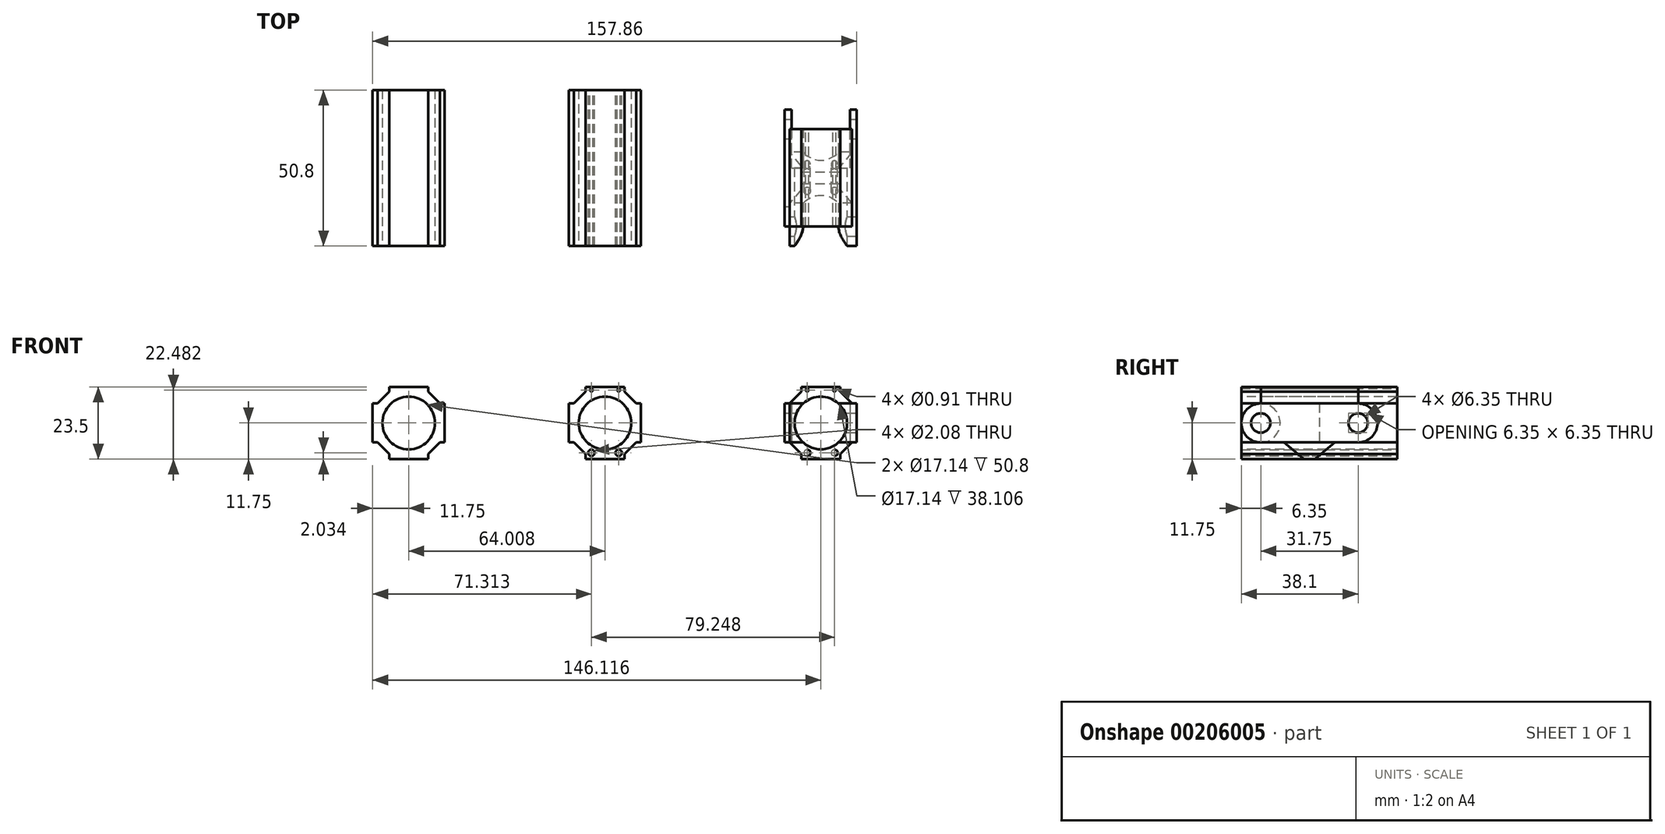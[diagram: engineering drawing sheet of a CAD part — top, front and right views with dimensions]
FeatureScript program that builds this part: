
annotation { "Feature Type Name" : "Feature", "Feature Type Description" : "" }
export const myFeature = defineFeature(function(context is Context, id is Id, definition is map)
    precondition{}
    {
        {
            var Q0;
            Q0=qCreatedBy(makeId("Front.planeOp"),FACE);
            var sketch = newSketch(context, id + "F0", { "sketchPlane" : qUnion([Q0])});
            skCircle(sketch, "E0", {"center": v(0, 0) * mm, "radius": 8.57 * mm});
            skCircle(sketch, "E1", {"center": v(0, 0) * mm, "radius": 11.11 * mm});
            skLineSegment(sketch, "E2", {"start": v(-13.77, 0) * mm, "end": v(14.8, 0) * mm, "construction": true});
            skLineSegment(sketch, "E3", {"start": v(0, 15.5) * mm, "end": v(0, -14.67) * mm, "construction": true});
            skLineSegment(sketch, "E4", {"start": v(-8.57, 0) * mm, "end": v(-8.57, -12.33) * mm, "construction": true});
            skLineSegment(sketch, "E5", {"start": v(8.57, 0) * mm, "end": v(8.57, -11.96) * mm, "construction": true});
            skLineSegment(sketch, "E6.bottom", {"start": v(-8.57, -6.35) * mm, "end": v(-11.75, -6.35) * mm});
            skLineSegment(sketch, "E6.top", {"start": v(-8.57, 6.35) * mm, "end": v(-11.75, 6.35) * mm});
            skLineSegment(sketch, "E6.left", {"start": v(-8.57, -6.35) * mm, "end": v(-8.57, 6.35) * mm});
            skLineSegment(sketch, "E6.right", {"start": v(-11.75, -6.35) * mm, "end": v(-11.75, 6.35) * mm});
            skPoint(sketch, "E7.oppositeSnap0", {"position": v(-10.16, 6.35) * mm});
            skLineSegment(sketch, "E7.bottom", {"start": v(8.57, -6.35) * mm, "end": v(11.75, -6.35) * mm});
            skLineSegment(sketch, "E7.top", {"start": v(8.57, 6.35) * mm, "end": v(11.75, 6.35) * mm});
            skLineSegment(sketch, "E7.left", {"start": v(8.57, -6.35) * mm, "end": v(8.57, 6.35) * mm});
            skLineSegment(sketch, "E7.right", {"start": v(11.75, -6.35) * mm, "end": v(11.75, 6.35) * mm});
            skLineSegment(sketch, "E8", {"start": v(0, 8.57) * mm, "end": v(9.91, 8.57) * mm, "construction": true});
            skLineSegment(sketch, "E9", {"start": v(0, -8.57) * mm, "end": v(9.95, -8.57) * mm, "construction": true});
            skLineSegment(sketch, "E10.bottom", {"start": v(6.35, 8.57) * mm, "end": v(-6.35, 8.57) * mm});
            skLineSegment(sketch, "E10.top", {"start": v(6.35, 11.75) * mm, "end": v(-6.35, 11.75) * mm});
            skLineSegment(sketch, "E10.left", {"start": v(6.35, 8.57) * mm, "end": v(6.35, 11.75) * mm});
            skLineSegment(sketch, "E10.right", {"start": v(-6.35, 8.57) * mm, "end": v(-6.35, 11.75) * mm});
            skPoint(sketch, "E11.oppositeSnap0", {"position": v(-6.35, 10.16) * mm});
            skLineSegment(sketch, "E11.bottom", {"start": v(6.35, -8.57) * mm, "end": v(-6.35, -8.57) * mm});
            skLineSegment(sketch, "E11.top", {"start": v(6.35, -11.75) * mm, "end": v(-6.35, -11.75) * mm});
            skLineSegment(sketch, "E11.left", {"start": v(6.35, -8.57) * mm, "end": v(6.35, -11.75) * mm});
            skLineSegment(sketch, "E11.right", {"start": v(-6.35, -8.57) * mm, "end": v(-6.35, -11.75) * mm});
            skLineSegment(sketch, "E12", {"start": v(-6.35, 10.16) * mm, "end": v(-10.16, 6.35) * mm});
            skLineSegment(sketch, "E13", {"start": v(-10.16, -6.35) * mm, "end": v(-6.35, -10.16) * mm});
            skLineSegment(sketch, "E14", {"start": v(6.35, -10.16) * mm, "end": v(10.16, -6.35) * mm});
            skLineSegment(sketch, "E15", {"start": v(6.35, 10.16) * mm, "end": v(10.16, 6.35) * mm});
            skSolve(sketch);
        }
        {
            var Q0;
            {var subQ4=sQuery(id+"F0.wireOp",EDGE,"E6.right");Q0=makeQuery(id+"F0.imprint","IMPRINT",FACE,{"disambiguationData":[TD([[makeQuery(id+"F0.imprint","IMPRINT",EDGE,{"derivedFrom":subQ4}),-1.0]])]});}
            var Q1;
            {var subQ5=sQuery(id+"F0.wireOp",EDGE,"E15");Q1=makeQuery(id+"F0.imprint","IMPRINT",FACE,{"disambiguationData":[TD([[makeQuery(id+"F0.imprint","IMPRINT",EDGE,{"derivedFrom":subQ5}),-1.0]])]});}
            var Q2;
            {var subQ0=sQuery(id+"F0.wireOp",EDGE,"E7.left");var subQ3=sQuery(id+"F0.wireOp",EDGE,"E0");var subQ4=makeQuery(id+"F0.imprint","INTERSECT",VERTEX,{"derivedFrom":[subQ3,subQ0]});Q2=makeQuery(id+"F0.imprint","IMPRINT",FACE,{"disambiguationData":[TD([[makeQuery(id+"F0.imprint","IMPRINT",EDGE,{"disambiguationData":[TD([[subQ4,1.0]])],"derivedFrom":subQ3}),-1.0]])]});}
            var Q3;
            {var subQ3=sQuery(id+"F0.wireOp",EDGE,"E0");var subQ9=sQuery(id+"F0.wireOp",EDGE,"E10.bottom");var subQ10=makeQuery(id+"F0.imprint","INTERSECT",VERTEX,{"derivedFrom":[subQ3,subQ9]});Q3=makeQuery(id+"F0.imprint","IMPRINT",FACE,{"disambiguationData":[TD([[makeQuery(id+"F0.imprint","IMPRINT",EDGE,{"disambiguationData":[TD([[subQ10,1.0]])],"derivedFrom":subQ3}),-1.0]])]});}
            var Q4;
            {var subQ0=sQuery(id+"F0.wireOp",EDGE,"E10.left");var subQ3=sQuery(id+"F0.wireOp",EDGE,"E1");var subQ4=makeQuery(id+"F0.imprint","INTERSECT",VERTEX,{"derivedFrom":[subQ3,subQ0]});Q4=makeQuery(id+"F0.imprint","IMPRINT",FACE,{"disambiguationData":[TD([[makeQuery(id+"F0.imprint","IMPRINT",EDGE,{"disambiguationData":[TD([[subQ4,-1.0]])],"derivedFrom":subQ3}),1.0]])]});}
            var Q5;
            {var subQ0=sQuery(id+"F0.wireOp",EDGE,"E10.top");Q5=makeQuery(id+"F0.imprint","IMPRINT",FACE,{"disambiguationData":[TD([[makeQuery(id+"F0.imprint","IMPRINT",EDGE,{"derivedFrom":subQ0}),1.0]])]});}
            var Q6;
            {var subQ5=sQuery(id+"F0.wireOp",EDGE,"E12");Q6=makeQuery(id+"F0.imprint","IMPRINT",FACE,{"disambiguationData":[TD([[makeQuery(id+"F0.imprint","IMPRINT",EDGE,{"derivedFrom":subQ5}),1.0]])]});}
            var Q7;
            {var subQ5=sQuery(id+"F0.wireOp",EDGE,"E0");var subQ9=sQuery(id+"F0.wireOp",EDGE,"E10.bottom");var subQ11=makeQuery(id+"F0.imprint","INTERSECT",VERTEX,{"derivedFrom":[subQ5,subQ9]});Q7=makeQuery(id+"F0.imprint","IMPRINT",FACE,{"disambiguationData":[TD([[makeQuery(id+"F0.imprint","IMPRINT",EDGE,{"disambiguationData":[TD([[subQ11,-1.0]])],"derivedFrom":subQ5}),-1.0]])]});}
            var Q8;
            {var subQ0=sQuery(id+"F0.wireOp",EDGE,"E6.left");var subQ7=sQuery(id+"F0.wireOp",EDGE,"E0");var subQ8=makeQuery(id+"F0.imprint","INTERSECT",VERTEX,{"derivedFrom":[subQ7,subQ0]});Q8=makeQuery(id+"F0.imprint","IMPRINT",FACE,{"disambiguationData":[TD([[makeQuery(id+"F0.imprint","IMPRINT",EDGE,{"disambiguationData":[TD([[subQ8,-1.0]])],"derivedFrom":subQ7}),-1.0]])]});}
            var Q9;
            {var subQ5=sQuery(id+"F0.wireOp",EDGE,"E13");Q9=makeQuery(id+"F0.imprint","IMPRINT",FACE,{"disambiguationData":[TD([[makeQuery(id+"F0.imprint","IMPRINT",EDGE,{"derivedFrom":subQ5}),1.0]])]});}
            var Q10;
            {var subQ4=sQuery(id+"F0.wireOp",EDGE,"E6.top");var subQ5=sQuery(id+"F0.wireOp",EDGE,"E1");var subQ6=makeQuery(id+"F0.imprint","INTERSECT",VERTEX,{"derivedFrom":[subQ5,subQ4]});Q10=makeQuery(id+"F0.imprint","IMPRINT",FACE,{"disambiguationData":[TD([[makeQuery(id+"F0.imprint","IMPRINT",EDGE,{"disambiguationData":[TD([[subQ6,-1.0]])],"derivedFrom":subQ5}),1.0]])]});}
            var Q11;
            {var subQ3=sQuery(id+"F0.wireOp",EDGE,"E1");var subQ6=sQuery(id+"F0.wireOp",EDGE,"E11.right");var subQ8=makeQuery(id+"F0.imprint","INTERSECT",VERTEX,{"derivedFrom":[subQ3,subQ6]});Q11=makeQuery(id+"F0.imprint","IMPRINT",FACE,{"disambiguationData":[TD([[makeQuery(id+"F0.imprint","IMPRINT",EDGE,{"disambiguationData":[TD([[subQ8,-1.0]])],"derivedFrom":subQ3}),1.0]])]});}
            var Q12;
            {var subQ1=sQuery(id+"F0.wireOp",EDGE,"E11.top");Q12=makeQuery(id+"F0.imprint","IMPRINT",FACE,{"disambiguationData":[TD([[makeQuery(id+"F0.imprint","IMPRINT",EDGE,{"derivedFrom":subQ1}),-1.0]])]});}
            var Q13;
            {var subQ5=sQuery(id+"F0.wireOp",EDGE,"E14");Q13=makeQuery(id+"F0.imprint","IMPRINT",FACE,{"disambiguationData":[TD([[makeQuery(id+"F0.imprint","IMPRINT",EDGE,{"derivedFrom":subQ5}),1.0]])]});}
            var Q14;
            {var subQ4=sQuery(id+"F0.wireOp",EDGE,"E1");var subQ6=sQuery(id+"F0.wireOp",EDGE,"E7.top");var subQ8=makeQuery(id+"F0.imprint","INTERSECT",VERTEX,{"derivedFrom":[subQ4,subQ6]});Q14=makeQuery(id+"F0.imprint","IMPRINT",FACE,{"disambiguationData":[TD([[makeQuery(id+"F0.imprint","IMPRINT",EDGE,{"disambiguationData":[TD([[subQ8,1.0]])],"derivedFrom":subQ4}),1.0]])]});}
            var Q15;
            {var subQ0=sQuery(id+"F0.wireOp",EDGE,"E7.right");Q15=makeQuery(id+"F0.imprint","IMPRINT",FACE,{"disambiguationData":[TD([[makeQuery(id+"F0.imprint","IMPRINT",EDGE,{"derivedFrom":subQ0}),1.0]])]});}
            extrude(context, id + "F1", {"entities" : qUnion([Q0, Q1, Q2, Q3, Q4, Q5, Q6, Q7, Q8, Q9, Q10, Q11, Q12, Q13, Q14, Q15]), "oppositeDirection" : true, "depth" : 50.8 * mm});
        }
        {
            var Q0;
            Q0=makeQuery(id+"F1.opExtrude","SWEPT_BODY",BODY,{"disambiguationData":[OSD([sQuery(id+"F0.wireOp",EDGE,"E0"),sQuery(id+"F0.wireOp",EDGE,"E6.bottom"),sQuery(id+"F0.wireOp",EDGE,"E6.top"),sQuery(id+"F0.wireOp",EDGE,"E6.right"),sQuery(id+"F0.wireOp",EDGE,"E7.bottom"),sQuery(id+"F0.wireOp",EDGE,"E7.top"),sQuery(id+"F0.wireOp",EDGE,"E7.right"),sQuery(id+"F0.wireOp",EDGE,"E10.top"),sQuery(id+"F0.wireOp",EDGE,"E10.left"),sQuery(id+"F0.wireOp",EDGE,"E10.right"),sQuery(id+"F0.wireOp",EDGE,"E11.top"),sQuery(id+"F0.wireOp",EDGE,"E11.left"),sQuery(id+"F0.wireOp",EDGE,"E11.right"),sQuery(id+"F0.wireOp",EDGE,"E12"),sQuery(id+"F0.wireOp",EDGE,"E13"),sQuery(id+"F0.wireOp",EDGE,"E14"),sQuery(id+"F0.wireOp",EDGE,"E15")])]});
            transform(context, id + "F2", {"entities" : qUnion([Q0]), "transformType" : TransformType.TRANSLATION_3D, "dx" : 64 * mm, "dy" : 0 * mm, "dz" : 0 * mm, "makeCopy" : true});
        }
        {
            var Q0;
            Q0=makeQuery(id+"F2.opPattern","COPY",FACE,{"derivedFrom":makeQuery(id+"F1.opExtrude","CAP_FACE",FACE,{"disambiguationData":[OSD([sQuery(id+"F0.wireOp",EDGE,"E0"),sQuery(id+"F0.wireOp",EDGE,"E6.bottom"),sQuery(id+"F0.wireOp",EDGE,"E6.top"),sQuery(id+"F0.wireOp",EDGE,"E6.right"),sQuery(id+"F0.wireOp",EDGE,"E7.bottom"),sQuery(id+"F0.wireOp",EDGE,"E7.top"),sQuery(id+"F0.wireOp",EDGE,"E7.right"),sQuery(id+"F0.wireOp",EDGE,"E10.top"),sQuery(id+"F0.wireOp",EDGE,"E10.left"),sQuery(id+"F0.wireOp",EDGE,"E10.right"),sQuery(id+"F0.wireOp",EDGE,"E11.top"),sQuery(id+"F0.wireOp",EDGE,"E11.left"),sQuery(id+"F0.wireOp",EDGE,"E11.right"),sQuery(id+"F0.wireOp",EDGE,"E12"),sQuery(id+"F0.wireOp",EDGE,"E13"),sQuery(id+"F0.wireOp",EDGE,"E14"),sQuery(id+"F0.wireOp",EDGE,"E15")])],"isStart":false}),"instanceName":"1"});
            var sketch = newSketch(context, id + "F3", { "sketchPlane" : qUnion([Q0])});
            skLineSegment(sketch, "E16", {"start": v(-64, 13.91) * mm, "end": v(-64, -14.22) * mm, "construction": true});
            skPoint(sketch, "E16.startSnap0", {"position": v(-64, 11.75) * mm});
            skPoint(sketch, "E16.endSnap0", {"position": v(-64, -11.75) * mm});
            skLineSegment(sketch, "E17", {"start": v(-64, -14.22) * mm, "end": v(-49, 0) * mm, "construction": true});
            skPoint(sketch, "E17.endSnap0", {"position": v(-52.26, 0) * mm});
            skLineSegment(sketch, "E18", {"start": v(-49, 0) * mm, "end": v(-78.43, 0) * mm, "construction": true});
            skLineSegment(sketch, "E19", {"start": v(-71.13, 10.73) * mm, "end": v(-56.78, 10.73) * mm, "construction": true});
            skLineSegment(sketch, "E20", {"start": v(-71, -9.72) * mm, "end": v(-56.68, -9.72) * mm, "construction": true});
            skLineSegment(sketch, "E21", {"start": v(-68.45, 12.56) * mm, "end": v(-68.45, -14.86) * mm, "construction": true});
            skLineSegment(sketch, "E22", {"start": v(-59.56, 12.76) * mm, "end": v(-59.56, -14.52) * mm, "construction": true});
            skCircle(sketch, "E23", {"center": v(-68.45, 10.73) * mm, "radius": 0.46 * mm});
            skCircle(sketch, "E24", {"center": v(-59.56, 10.73) * mm, "radius": 0.46 * mm});
            skCircle(sketch, "E25", {"center": v(-68.45, -9.72) * mm, "radius": 1.04 * mm});
            skCircle(sketch, "E26", {"center": v(-59.56, -9.72) * mm, "radius": 1.04 * mm});
            skSolve(sketch);
        }
        {
            var Q0;
            Q0 = qSketchRegion(id + "F3", true);
            extrude(context, id + "F4", {"entities" : qUnion([Q0]), "operationType" : NewBodyOperationType.REMOVE, "endBound" : BoundingType.THROUGH_ALL, "oppositeDirection" : true, "depth" : 25.4 * mm});
        }
        {
            var Q0;
            Q0=makeQuery(id+"F2.opPattern","COPY",BODY,{"derivedFrom":makeQuery(id+"F1.opExtrude","SWEPT_BODY",BODY,{"disambiguationData":[OSD([sQuery(id+"F0.wireOp",EDGE,"E0"),sQuery(id+"F0.wireOp",EDGE,"E6.bottom"),sQuery(id+"F0.wireOp",EDGE,"E6.top"),sQuery(id+"F0.wireOp",EDGE,"E6.right"),sQuery(id+"F0.wireOp",EDGE,"E7.bottom"),sQuery(id+"F0.wireOp",EDGE,"E7.top"),sQuery(id+"F0.wireOp",EDGE,"E7.right"),sQuery(id+"F0.wireOp",EDGE,"E10.top"),sQuery(id+"F0.wireOp",EDGE,"E10.left"),sQuery(id+"F0.wireOp",EDGE,"E10.right"),sQuery(id+"F0.wireOp",EDGE,"E11.top"),sQuery(id+"F0.wireOp",EDGE,"E11.left"),sQuery(id+"F0.wireOp",EDGE,"E11.right"),sQuery(id+"F0.wireOp",EDGE,"E12"),sQuery(id+"F0.wireOp",EDGE,"E13"),sQuery(id+"F0.wireOp",EDGE,"E14"),sQuery(id+"F0.wireOp",EDGE,"E15")])]}),"instanceName":"1"});
            transform(context, id + "F5", {"entities" : qUnion([Q0]), "transformType" : TransformType.TRANSLATION_3D, "dx" : 70.36 * mm, "dy" : 0 * mm, "dz" : 0 * mm, "makeCopy" : true});
        }
        {
            var Q0;
            Q0=makeQuery(id+"F5.opPattern","COPY",FACE,{"derivedFrom":makeQuery(id+"F2.opPattern","COPY",FACE,{"derivedFrom":makeQuery(id+"F1.opExtrude","SWEPT_FACE",FACE,{"disambiguationData":[OSD([sQuery(id+"F0.wireOp",EDGE,"E6.right")])]}),"instanceName":"1"}),"instanceName":"1"});
            var sketch = newSketch(context, id + "F6", { "sketchPlane" : qUnion([Q0])});
            skLineSegment(sketch, "E27", {"start": v(-58.56, 0) * mm, "end": v(8.02, 0) * mm, "construction": true});
            skPoint(sketch, "E27.startSnap0", {"position": v(-50.8, 0) * mm});
            skLineSegment(sketch, "E28", {"start": v(8.02, 0) * mm, "end": v(-6.35, -6.35) * mm, "construction": true});
            skLineSegment(sketch, "E29", {"start": v(-6.35, -6.35) * mm, "end": v(-6.35, 6.35) * mm, "construction": true});
            skLineSegment(sketch, "E30", {"start": v(-6.35, 6.35) * mm, "end": v(-38.1, -6.35) * mm, "construction": true});
            skLineSegment(sketch, "E31", {"start": v(-38.1, -6.35) * mm, "end": v(-38.1, 6.35) * mm, "construction": true});
            skCircle(sketch, "E32", {"center": v(-38.1, 0) * mm, "radius": 6.35 * mm});
            skCircle(sketch, "E33", {"center": v(-6.35, 0) * mm, "radius": 6.35 * mm});
            skLineSegment(sketch, "E34", {"start": v(-38.1, 0) * mm, "end": v(-38.1, 26.2) * mm});
            skLineSegment(sketch, "E35", {"start": v(-38.1, 26.2) * mm, "end": v(-54.63, 26.2) * mm});
            skLineSegment(sketch, "E36", {"start": v(-54.63, 26.2) * mm, "end": v(-54.63, -15.63) * mm});
            skLineSegment(sketch, "E37", {"start": v(-54.63, -15.63) * mm, "end": v(-19.48, -15.63) * mm});
            skLineSegment(sketch, "E38", {"start": v(-19.48, -15.63) * mm, "end": v(-38.1, 0) * mm});
            skLineSegment(sketch, "E39", {"start": v(-6.35, 6.35) * mm, "end": v(-6.35, 21.02) * mm});
            skLineSegment(sketch, "E40", {"start": v(-6.35, 21.02) * mm, "end": v(12.9, 21.02) * mm});
            skLineSegment(sketch, "E41", {"start": v(12.9, 21.02) * mm, "end": v(12.9, -12.91) * mm});
            skLineSegment(sketch, "E42", {"start": v(12.9, -12.91) * mm, "end": v(-21.74, -12.91) * mm});
            skLineSegment(sketch, "E43", {"start": v(-21.74, -12.91) * mm, "end": v(-6.35, 0) * mm});
            skLineSegment(sketch, "E44", {"start": v(-38.1, -6.35) * mm, "end": v(-30.53, -6.35) * mm});
            skLineSegment(sketch, "E45", {"start": v(-6.35, -6.35) * mm, "end": v(-13.92, -6.35) * mm});
            skSolve(sketch);
        }
        {
            var Q0;
            {var subQ1=sQuery(id+"F6.wireOp",EDGE,"E35");Q0=makeQuery(id+"F6.imprint","IMPRINT",FACE,{"disambiguationData":[TD([[makeQuery(id+"F6.imprint","IMPRINT",EDGE,{"derivedFrom":subQ1}),1.0]])]});}
            var Q1;
            {var subQ1=sQuery(id+"F0.wireOp",EDGE,"E6.right");var subQ6=makeQuery(id+"F5.opPattern","COPY",EDGE,{"derivedFrom":makeQuery(id+"F2.opPattern","COPY",EDGE,{"derivedFrom":makeQuery(id+"F1.opExtrude","CAP_EDGE",EDGE,{"disambiguationData":[OSD([subQ1])],"isStart":false}),"instanceName":"1"}),"instanceName":"1"});Q1=makeQuery(id+"F6.imprint","IMPRINT",FACE,{"disambiguationData":[TD([[makeQuery(id+"F6.imprint","IMPRINT",EDGE,{"derivedFrom":subQ6}),-1.0]])]});}
            var Q2;
            {var subQ7=sQuery(id+"F6.wireOp",EDGE,"E39");Q2=makeQuery(id+"F6.imprint","IMPRINT",FACE,{"disambiguationData":[TD([[makeQuery(id+"F6.imprint","IMPRINT",EDGE,{"derivedFrom":subQ7}),-1.0]])]});}
            var Q3;
            {var subQ0=sQuery(id+"F6.wireOp",EDGE,"E33");var subQ1=sQuery(id+"F0.wireOp",EDGE,"E6.right");var subQ4=makeQuery(id+"F5.opPattern","COPY",EDGE,{"derivedFrom":makeQuery(id+"F2.opPattern","COPY",EDGE,{"derivedFrom":makeQuery(id+"F1.opExtrude","CAP_EDGE",EDGE,{"disambiguationData":[OSD([subQ1])],"isStart":true}),"instanceName":"1"}),"instanceName":"1"});var subQ5=makeQuery(id+"F6.imprint","INTERSECT",VERTEX,{"derivedFrom":[subQ4,subQ0]});Q3=makeQuery(id+"F6.imprint","IMPRINT",FACE,{"disambiguationData":[TD([[makeQuery(id+"F6.imprint","IMPRINT",EDGE,{"disambiguationData":[TD([[subQ5,1.0]])],"derivedFrom":subQ4}),1.0]])]});}
            var Q4;
            {var subQ0=sQuery(id+"F6.wireOp",EDGE,"E33");var subQ1=sQuery(id+"F0.wireOp",EDGE,"E6.right");var subQ4=makeQuery(id+"F5.opPattern","COPY",EDGE,{"derivedFrom":makeQuery(id+"F2.opPattern","COPY",EDGE,{"derivedFrom":makeQuery(id+"F1.opExtrude","CAP_EDGE",EDGE,{"disambiguationData":[OSD([subQ1])],"isStart":true}),"instanceName":"1"}),"instanceName":"1"});var subQ5=makeQuery(id+"F6.imprint","INTERSECT",VERTEX,{"derivedFrom":[subQ4,subQ0]});Q4=makeQuery(id+"F6.imprint","IMPRINT",FACE,{"disambiguationData":[TD([[makeQuery(id+"F6.imprint","IMPRINT",EDGE,{"disambiguationData":[TD([[subQ5,-1.0]])],"derivedFrom":subQ4}),1.0]])]});}
            extrude(context, id + "F7", {"entities" : qUnion([Q0, Q1, Q2, Q3, Q4]), "operationType" : NewBodyOperationType.REMOVE, "oppositeDirection" : true, "depth" : 25.4 * mm});
        }
        {
            var Q0;
            Q0=makeQuery(id+"F5.opPattern","COPY",FACE,{"derivedFrom":makeQuery(id+"F2.opPattern","COPY",FACE,{"derivedFrom":makeQuery(id+"F1.opExtrude","SWEPT_FACE",FACE,{"disambiguationData":[OSD([sQuery(id+"F0.wireOp",EDGE,"E7.right")])]}),"instanceName":"1"}),"instanceName":"1"});
            var sketch = newSketch(context, id + "F8", { "sketchPlane" : qUnion([Q0])});
            skCircle(sketch, "E46", {"center": v(6.35, 0) * mm, "radius": 3.18 * mm});
            skCircle(sketch, "E47", {"center": v(38.1, 0) * mm, "radius": 3.18 * mm});
            skSolve(sketch);
        }
        {
            var Q0;
            Q0 = qSketchRegion(id + "F8", true);
            extrude(context, id + "F9", {"entities" : qUnion([Q0]), "operationType" : NewBodyOperationType.REMOVE, "oppositeDirection" : true, "depth" : 25.4 * mm});
        }
        {
            var Q0;
            Q0=makeQuery(id+"F7.boolean.opBoolean","COPY",FACE,{"derivedFrom":makeQuery(id+"F7.opExtrude","SWEPT_FACE",FACE,{"disambiguationData":[OSD([sQuery(id+"F6.wireOp",EDGE,"E34")])]})});
            var sketch = newSketch(context, id + "F10", { "sketchPlane" : qUnion([Q0])});
            skLineSegment(sketch, "E48.bottom", {"start": v(-143.9, 6.35) * mm, "end": v(-124.84, 6.35) * mm});
            skLineSegment(sketch, "E48.top", {"start": v(-143.9, -6.35) * mm, "end": v(-124.84, -6.35) * mm});
            skLineSegment(sketch, "E48.left", {"start": v(-143.9, 6.35) * mm, "end": v(-143.9, -6.35) * mm});
            skLineSegment(sketch, "E48.right", {"start": v(-124.84, 6.35) * mm, "end": v(-124.84, -6.35) * mm});
            skLineSegment(sketch, "E49", {"start": v(-134.37, 13.93) * mm, "end": v(-134.37, -15.19) * mm, "construction": true});
            skPoint(sketch, "E49.startSnap0", {"position": v(-134.37, 11.75) * mm});
            skSolve(sketch);
        }
        {
            var Q0;
            Q0 = qSketchRegion(id + "F10", true);
            extrude(context, id + "F11", {"entities" : qUnion([Q0]), "operationType" : NewBodyOperationType.REMOVE, "depth" : 25.4 * mm});
        }
        {
            var Q0;
            Q0=makeQuery(id+"F11.boolean.opBoolean","MERGE",FACE,{"derivedFrom":[makeQuery(id+"F7.boolean.opBoolean","COPY",FACE,{"derivedFrom":makeQuery(id+"F7.opExtrude","SWEPT_FACE",FACE,{"disambiguationData":[OSD([sQuery(id+"F6.wireOp",EDGE,"E34")])]})}),makeQuery(id+"F11.opExtrude","CAP_FACE",FACE,{"disambiguationData":[OSD([sQuery(id+"F10.wireOp",EDGE,"E48.bottom"),sQuery(id+"F10.wireOp",EDGE,"E48.top"),sQuery(id+"F10.wireOp",EDGE,"E48.left"),sQuery(id+"F10.wireOp",EDGE,"E48.right")])],"isStart":true})]});
            var sketch = newSketch(context, id + "F12", { "sketchPlane" : qUnion([Q0])});
            skLineSegment(sketch, "E50.bottom", {"start": v(-124.84, 6.35) * mm, "end": v(-143.9, 6.35) * mm});
            skLineSegment(sketch, "E50.top", {"start": v(-124.84, -6.35) * mm, "end": v(-143.9, -6.35) * mm});
            skLineSegment(sketch, "E50.left", {"start": v(-124.84, 6.35) * mm, "end": v(-124.84, -6.35) * mm});
            skLineSegment(sketch, "E50.right", {"start": v(-143.9, 6.35) * mm, "end": v(-143.9, -6.35) * mm});
            skSolve(sketch);
        }
        {
            var Q0;
            Q0 = qSketchRegion(id + "F12", true);
            extrude(context, id + "F13", {"entities" : qUnion([Q0]), "operationType" : NewBodyOperationType.REMOVE, "oppositeDirection" : true, "depth" : 12.7 * mm});
        }
        {
            var Q0;
            Q0=makeQuery(id+"F5.opPattern","COPY",FACE,{"derivedFrom":makeQuery(id+"F2.opPattern","COPY",FACE,{"derivedFrom":makeQuery(id+"F1.opExtrude","SWEPT_FACE",FACE,{"disambiguationData":[OSD([sQuery(id+"F0.wireOp",EDGE,"E6.right")])]}),"instanceName":"1"}),"instanceName":"1"});
            var sketch = newSketch(context, id + "F14", { "sketchPlane" : qUnion([Q0])});
            skCircle(sketch, "E51", {"center": v(-6.35, 0) * mm, "radius": 6.35 * mm});
            skSolve(sketch);
        }
        {
            var Q0;
            Q0 = qSketchRegion(id + "F14", true);
            extrude(context, id + "F15", {"entities" : qUnion([Q0]), "operationType" : NewBodyOperationType.REMOVE, "oppositeDirection" : true, "depth" : 1.59 * mm});
        }
    });
